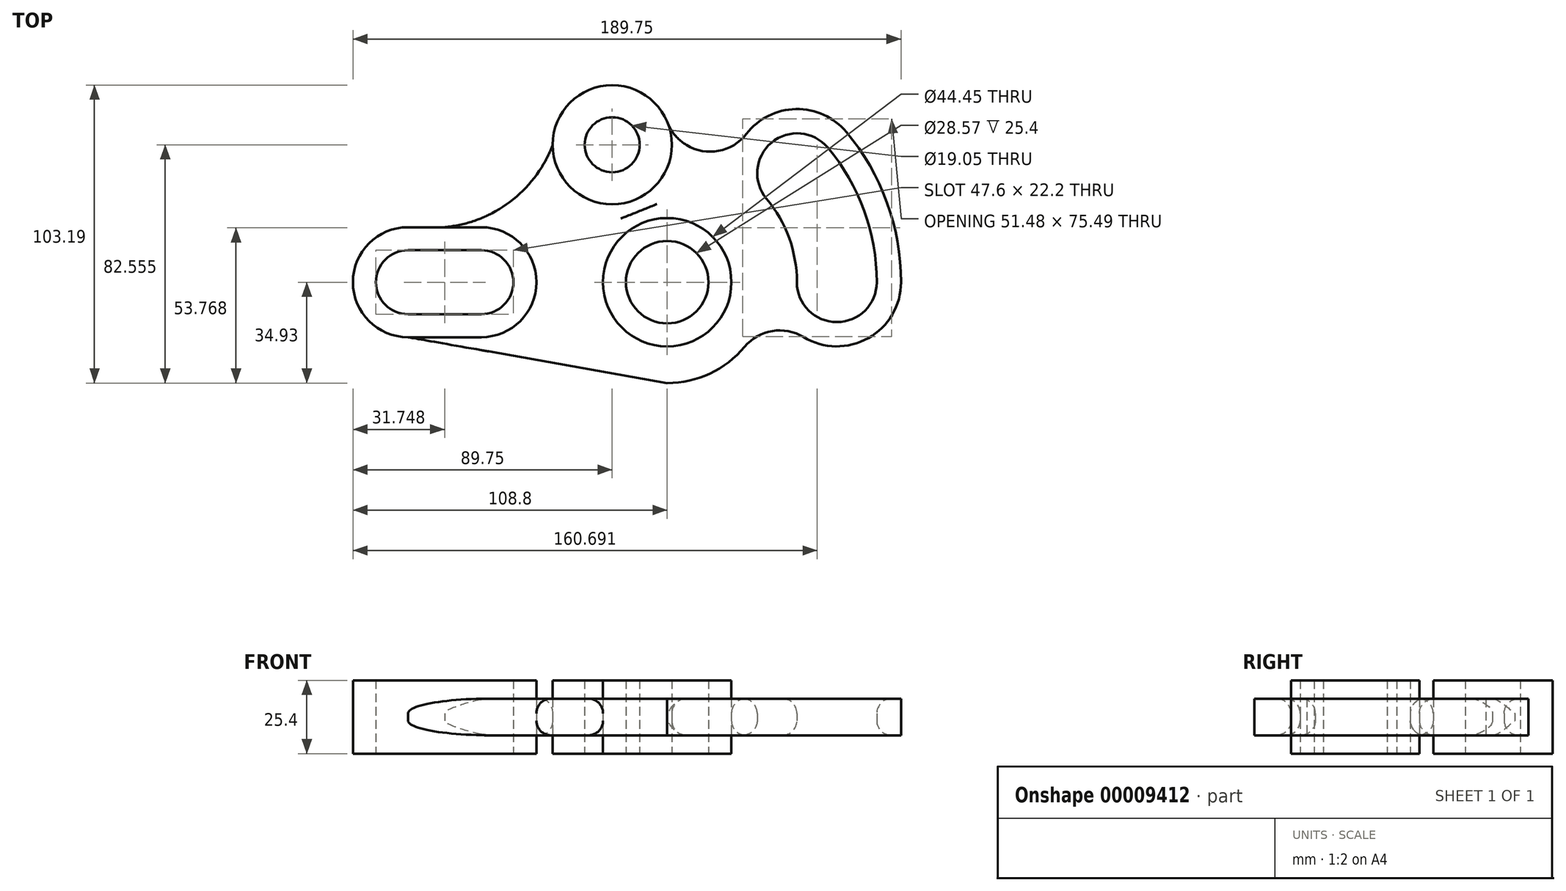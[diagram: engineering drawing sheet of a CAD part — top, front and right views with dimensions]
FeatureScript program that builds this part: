
annotation { "Feature Type Name" : "Feature", "Feature Type Description" : "" }
export const myFeature = defineFeature(function(context is Context, id is Id, definition is map)
    precondition{}
    {
        {
            var Q0;
            Q0=qCreatedBy(makeId("Top.planeOp"),FACE);
            var sketch = newSketch(context, id + "F0", { "sketchPlane" : qUnion([Q0])});
            skCircle(sketch, "E0", {"center": v(0, 0) * mm, "radius": 14.29 * mm});
            skLineSegment(sketch, "E1", {"start": v(112.06, 0) * mm, "end": v(-173.36, 0) * mm, "construction": true});
            skLineSegment(sketch, "E2", {"start": v(0, 93.44) * mm, "end": v(0, -67.37) * mm, "construction": true});
            skLineSegment(sketch, "E3", {"start": v(0, 0) * mm, "end": v(97.77, 82.04) * mm, "construction": true});
            skCircle(sketch, "E4", {"center": v(0, 0) * mm, "radius": 22.23 * mm});
            skArc(sketch, "E5", {"start": v(-89.75, 11.1) * mm, "mid": v(-100.85, 0) * mm, "end": v(-89.75, -11.1) * mm});
            skArc(sketch, "E6", {"start": v(-64.35, -11.1) * mm, "mid": v(-53.25, 0) * mm, "end": v(-64.35, 11.1) * mm});
            skLineSegment(sketch, "E7", {"start": v(-89.75, 11.1) * mm, "end": v(-64.35, 11.1) * mm});
            skLineSegment(sketch, "E8", {"start": v(-89.75, -11.1) * mm, "end": v(-64.35, -11.1) * mm});
            skArc(sketch, "E9.0", {"start": v(-89.75, 19.05) * mm, "mid": v(-108.8, 0) * mm, "end": v(-89.75, -19.05) * mm});
            skLineSegment(sketch, "E9.1", {"start": v(-89.75, 19.05) * mm, "end": v(-64.35, 19.05) * mm});
            skArc(sketch, "E9.2", {"start": v(-64.35, -19.05) * mm, "mid": v(-45.3, 0) * mm, "end": v(-64.35, 19.05) * mm});
            skLineSegment(sketch, "E9.3", {"start": v(-89.75, -19.05) * mm, "end": v(-64.35, -19.05) * mm});
            skCircle(sketch, "E10", {"center": v(-19.05, 47.62) * mm, "radius": 9.53 * mm});
            skCircle(sketch, "E11", {"center": v(-19.05, 47.62) * mm, "radius": 20.64 * mm});
            skArc(sketch, "E12", {"start": v(-77.05, 19.05) * mm, "mid": v(-54.3, 27.94) * mm, "end": v(-39.69, 47.5) * mm});
            skArc(sketch, "E13", {"start": v(44.9, 0) * mm, "mid": v(58.72, -13.83) * mm, "end": v(72.55, 0) * mm});
            skArc(sketch, "E14", {"start": v(58.72, 0) * mm, "mid": v(55.18, 20.09) * mm, "end": v(44.99, 37.75) * mm, "construction": true});
            skArc(sketch, "E15", {"start": v(55.58, 46.64) * mm, "mid": v(36.1, 48.34) * mm, "end": v(34.4, 28.86) * mm});
            skArc(sketch, "E16", {"start": v(72.55, 0) * mm, "mid": v(68.18, 24.81) * mm, "end": v(55.58, 46.64) * mm});
            skArc(sketch, "E17", {"start": v(44.9, 0) * mm, "mid": v(42.19, 15.36) * mm, "end": v(34.4, 28.86) * mm});
            skArc(sketch, "E18.1", {"start": v(80.95, 0) * mm, "mid": v(76.07, 27.69) * mm, "end": v(62.01, 52.03) * mm});
            skArc(sketch, "E18.2", {"start": v(47.2, -19) * mm, "mid": v(69.63, -19.36) * mm, "end": v(80.95, 0) * mm});
            skLineSegment(sketch, "E19", {"start": v(-95.43, 47.62) * mm, "end": v(131.54, 47.5) * mm, "construction": true});
            skArc(sketch, "E20", {"start": v(0, 55.58) * mm, "mid": v(12.48, 45.41) * mm, "end": v(27.43, 51.37) * mm});
            skArc(sketch, "E21", {"start": v(62.01, 52.03) * mm, "mid": v(44.56, 59.97) * mm, "end": v(27.43, 51.37) * mm});
            skLineSegment(sketch, "E22", {"start": v(-89.75, -19.05) * mm, "end": v(0, -34.93) * mm});
            skArc(sketch, "E23", {"start": v(47.2, -19) * mm, "mid": v(36.37, -16.92) * mm, "end": v(26.8, -22.4) * mm});
            skArc(sketch, "E24", {"start": v(0, -34.93) * mm, "mid": v(14.79, -31.64) * mm, "end": v(26.8, -22.4) * mm});
            skSolve(sketch);
        }
        {
            var Q0;
            Q0=makeQuery(id+"F0.imprint","IMPRINT",FACE,{"disambiguationData":[TD([[makeQuery(id+"F0.imprint","IMPRINT",EDGE,{"derivedFrom":sQuery(id+"F0.wireOp",EDGE,"E10")}),-1.0]])]});
            var Q1;
            Q1=makeQuery(id+"F0.imprint","IMPRINT",FACE,{"disambiguationData":[TD([[makeQuery(id+"F0.imprint","IMPRINT",EDGE,{"derivedFrom":sQuery(id+"F0.wireOp",EDGE,"E5")}),-1.0]])]});
            var Q2;
            Q2=makeQuery(id+"F0.imprint","IMPRINT",FACE,{"disambiguationData":[TD([[makeQuery(id+"F0.imprint","IMPRINT",EDGE,{"derivedFrom":sQuery(id+"F0.wireOp",EDGE,"E0")}),-1.0]])]});
            extrude(context, id + "F1", {"entities" : qUnion([Q0, Q1, Q2]), "endBound" : BoundingType.SYMMETRIC, "depth" : 25.4 * mm});
        }
        {
            var Q0;
            Q0=makeQuery(id+"F0.imprint","IMPRINT",FACE,{"disambiguationData":[TD([[makeQuery(id+"F0.imprint","IMPRINT",EDGE,{"derivedFrom":sQuery(id+"F0.wireOp",EDGE,"E4")}),-1.0]])]});
            extrude(context, id + "F2", {"entities" : qUnion([Q0]), "endBound" : BoundingType.SYMMETRIC, "depth" : 12.7 * mm});
        }
        {
            var Q0;
            Q0=makeQuery(id+"F2.opExtrude","CAP_EDGE",EDGE,{"disambiguationData":[OSD([sQuery(id+"F0.wireOp",EDGE,"E11")])],"isStart":false});
            var Q1;
            Q1=makeQuery(id+"F2.opExtrude","CAP_EDGE",EDGE,{"disambiguationData":[OSD([sQuery(id+"F0.wireOp",EDGE,"E9.2")])],"isStart":false});
            var Q2;
            Q2=makeQuery(id+"F2.opExtrude","CAP_EDGE",EDGE,{"disambiguationData":[OSD([sQuery(id+"F0.wireOp",EDGE,"E4")])],"isStart":false});
            var Q3;
            Q3=makeQuery(id+"F2.opExtrude","CAP_EDGE",EDGE,{"disambiguationData":[OSD([sQuery(id+"F0.wireOp",EDGE,"E9.2")])],"isStart":true});
            var Q4;
            Q4=makeQuery(id+"F2.opExtrude","CAP_EDGE",EDGE,{"disambiguationData":[OSD([sQuery(id+"F0.wireOp",EDGE,"E4")])],"isStart":true});
            var Q5;
            Q5=makeQuery(id+"F2.opExtrude","CAP_EDGE",EDGE,{"disambiguationData":[OSD([sQuery(id+"F0.wireOp",EDGE,"E11")])],"isStart":true});
            fillet(context, id + "F3", {"entities" : qUnion([Q0, Q1, Q2, Q3, Q4, Q5]), "radius" : 5.08 * mm, "tangentPropagation" : true, "allowEdgeOverflow" : false});
        }
        {
            var Q0;
            Q0=makeQuery(id+"F2.opExtrude","CAP_EDGE",EDGE,{"disambiguationData":[OSD([sQuery(id+"F0.wireOp",EDGE,"E13")])],"isStart":true});
            var Q1;
            Q1=makeQuery(id+"F2.opExtrude","CAP_EDGE",EDGE,{"disambiguationData":[OSD([sQuery(id+"F0.wireOp",EDGE,"E17")])],"isStart":false});
            fillet(context, id + "F4", {"entities" : qUnion([Q0, Q1]), "radius" : 5.08 * mm, "tangentPropagation" : true, "allowEdgeOverflow" : false});
        }
    });
